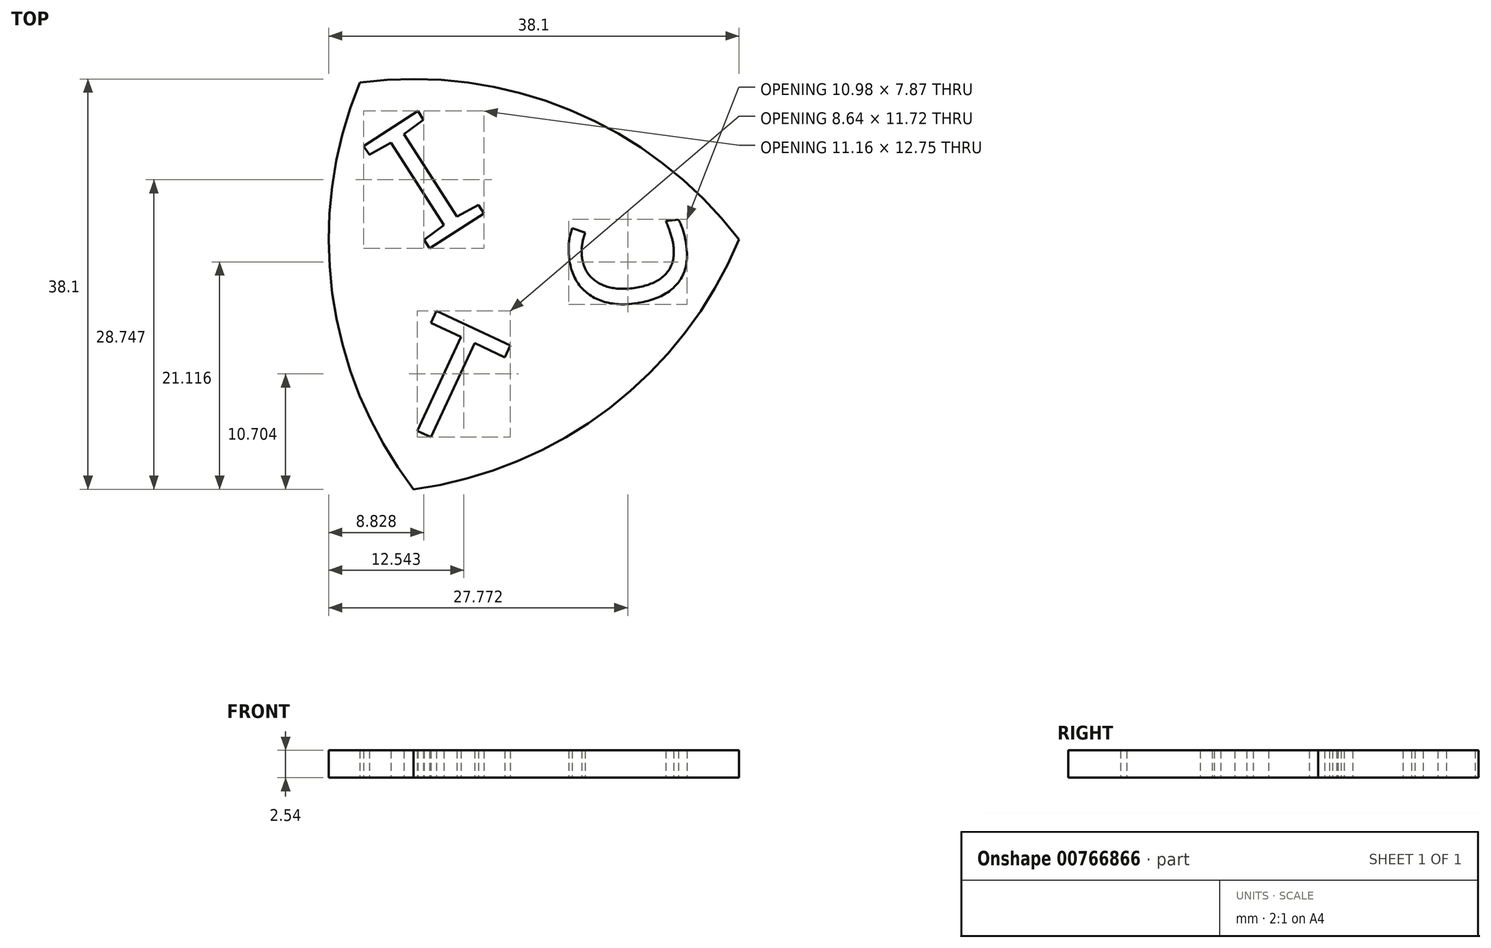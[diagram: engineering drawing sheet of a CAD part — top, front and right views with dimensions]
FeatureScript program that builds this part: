
annotation { "Feature Type Name" : "Feature", "Feature Type Description" : "" }
export const myFeature = defineFeature(function(context is Context, id is Id, definition is map)
    precondition{}
    {
        {
            var Q0;
            Q0=qCreatedBy(makeId("Top.planeOp"),FACE);
            var sketch = newSketch(context, id + "F0", { "sketchPlane" : qUnion([Q0])});
            skCircle(sketch, "E0", {"center": v(0, 0) * mm, "radius": 38.1 * mm});
            skSolve(sketch);
        }
        {
            var Q0;
            Q0=qCreatedBy(makeId("Top.planeOp"),FACE);
            var sketch = newSketch(context, id + "F1", { "sketchPlane" : qUnion([Q0])});
            skCircle(sketch, "E1", {"center": v(-35.2, 14.57) * mm, "radius": 38.1 * mm});
            skSolve(sketch);
        }
        {
            var Q0;
            Q0=qCreatedBy(makeId("Top.planeOp"),FACE);
            var sketch = newSketch(context, id + "F2", { "sketchPlane" : qUnion([Q0])});
            skCircle(sketch, "E2", {"center": v(-30.22, -23.2) * mm, "radius": 38.1 * mm});
            skSolve(sketch);
        }
        {
            var Q0;
            Q0=makeQuery(id+"F2.imprint","IMPRINT",FACE,{"disambiguationData":[TD([[makeQuery(id+"F2.imprint","IMPRINT",EDGE,{"derivedFrom":sQuery(id+"F2.wireOp",EDGE,"E2")}),1.0]])]});
            var Q1;
            Q1=makeQuery(id+"F1.imprint","IMPRINT",FACE,{"disambiguationData":[TD([[makeQuery(id+"F1.imprint","IMPRINT",EDGE,{"derivedFrom":sQuery(id+"F1.wireOp",EDGE,"E1")}),1.0]])]});
            var Q2;
            Q2=makeQuery(id+"F0.imprint","IMPRINT",FACE,{"disambiguationData":[TD([[makeQuery(id+"F0.imprint","IMPRINT",EDGE,{"derivedFrom":sQuery(id+"F0.wireOp",EDGE,"E0")}),1.0]])]});
            extrude(context, id + "F3", {"entities" : qUnion([Q0, Q1, Q2]), "depth" : 2.54 * mm, "offsetDistance" : 25.4 * mm});
        }
        {
            var Q0;
            Q0=makeQuery(id+"F3.opExtrude","SWEPT_BODY",BODY,{"disambiguationData":[OSD([sQuery(id+"F2.wireOp",EDGE,"E2")])]});
            var Q1;
            Q1=makeQuery(id+"F3.opExtrude","SWEPT_BODY",BODY,{"disambiguationData":[OSD([sQuery(id+"F1.wireOp",EDGE,"E1")])]});
            var Q2;
            Q2=makeQuery(id+"F3.opExtrude","SWEPT_BODY",BODY,{"disambiguationData":[OSD([sQuery(id+"F0.wireOp",EDGE,"E0")])]});
            booleanBodies(context, id + "F4", {"operationType" : BooleanOperationType.INTERSECTION, "tools" : qUnion([Q0, Q1, Q2])});
        }
        {
            var Q0;
            Q0=qCreatedBy(makeId("Top.planeOp"),FACE);
            var sketch = newSketch(context, id + "F5", { "sketchPlane" : qUnion([Q0])});
            skText(sketch, "E3", { "text": "C", "fontName": "DroidSansMono.ttf"});
            skText(sketch, "E4", { "text": "I", "fontName": "DroidSansMono.ttf"});
            skText(sketch, "E5", { "text": "T", "fontName": "DroidSansMono.ttf"});
            const initialGuessF5  = {"E3": [-0.00434, -0.00623, -0.12316, 0.99239, 0.01073], "E4": [-0.0302, -0.00177, 0.84102, 0.54101, 0.0114], "E5": [-0.03337, -0.01614, 0.9063, -0.42262, 0.01093]};
            skSetInitialGuess(sketch, initialGuessF5);
            skSolve(sketch);
        }
        {
            var Q0;
            Q0 = qSketchRegion(id + "F5", true);
            extrude(context, id + "F6", {"entities" : qUnion([Q0]), "depth" : 2.54 * mm, "offsetDistance" : 25.4 * mm});
        }
        {
            var Q0;
            Q0=makeQuery(id+"F6.opExtrude","SWEPT_BODY",BODY,{"disambiguationData":[OSD([sQuery(id+"F5.wireOp",EDGE,"E3.sketch_text.stroke-0"),sQuery(id+"F5.wireOp",EDGE,"E3.sketch_text.stroke-1"),sQuery(id+"F5.wireOp",EDGE,"E3.sketch_text.stroke-2"),sQuery(id+"F5.wireOp",EDGE,"E3.sketch_text.stroke-3"),sQuery(id+"F5.wireOp",EDGE,"E3.sketch_text.stroke-4"),sQuery(id+"F5.wireOp",EDGE,"E3.sketch_text.stroke-5"),sQuery(id+"F5.wireOp",EDGE,"E3.sketch_text.stroke-6"),sQuery(id+"F5.wireOp",EDGE,"E3.sketch_text.stroke-7"),sQuery(id+"F5.wireOp",EDGE,"E3.sketch_text.stroke-8"),sQuery(id+"F5.wireOp",EDGE,"E3.sketch_text.stroke-9"),sQuery(id+"F5.wireOp",EDGE,"E3.sketch_text.stroke-10"),sQuery(id+"F5.wireOp",EDGE,"E3.sketch_text.stroke-11"),sQuery(id+"F5.wireOp",EDGE,"E3.sketch_text.stroke-12"),sQuery(id+"F5.wireOp",EDGE,"E3.sketch_text.stroke-13")])]});
            var Q1;
            Q1=makeQuery(id+"F6.opExtrude","SWEPT_BODY",BODY,{"disambiguationData":[OSD([sQuery(id+"F5.wireOp",EDGE,"E5.sketch_text.stroke-0"),sQuery(id+"F5.wireOp",EDGE,"E5.sketch_text.stroke-1"),sQuery(id+"F5.wireOp",EDGE,"E5.sketch_text.stroke-2"),sQuery(id+"F5.wireOp",EDGE,"E5.sketch_text.stroke-3"),sQuery(id+"F5.wireOp",EDGE,"E5.sketch_text.stroke-4"),sQuery(id+"F5.wireOp",EDGE,"E5.sketch_text.stroke-5"),sQuery(id+"F5.wireOp",EDGE,"E5.sketch_text.stroke-6"),sQuery(id+"F5.wireOp",EDGE,"E5.sketch_text.stroke-7")])]});
            var Q2;
            Q2=makeQuery(id+"F6.opExtrude","SWEPT_BODY",BODY,{"disambiguationData":[OSD([sQuery(id+"F5.wireOp",EDGE,"E4.sketch_text.stroke-0"),sQuery(id+"F5.wireOp",EDGE,"E4.sketch_text.stroke-1"),sQuery(id+"F5.wireOp",EDGE,"E4.sketch_text.stroke-2"),sQuery(id+"F5.wireOp",EDGE,"E4.sketch_text.stroke-3"),sQuery(id+"F5.wireOp",EDGE,"E4.sketch_text.stroke-4"),sQuery(id+"F5.wireOp",EDGE,"E4.sketch_text.stroke-5"),sQuery(id+"F5.wireOp",EDGE,"E4.sketch_text.stroke-6"),sQuery(id+"F5.wireOp",EDGE,"E4.sketch_text.stroke-7"),sQuery(id+"F5.wireOp",EDGE,"E4.sketch_text.stroke-8"),sQuery(id+"F5.wireOp",EDGE,"E4.sketch_text.stroke-9"),sQuery(id+"F5.wireOp",EDGE,"E4.sketch_text.stroke-10"),sQuery(id+"F5.wireOp",EDGE,"E4.sketch_text.stroke-11")])]});
            var Q3;
            Q3=makeQuery(id+"F4.opBoolean","INTERSECT",BODY,{"derivedFrom":[makeQuery(id+"F3.opExtrude","SWEPT_BODY",BODY,{"disambiguationData":[OSD([sQuery(id+"F0.wireOp",EDGE,"E0")])]}),makeQuery(id+"F3.opExtrude","SWEPT_BODY",BODY,{"disambiguationData":[OSD([sQuery(id+"F1.wireOp",EDGE,"E1")])]}),makeQuery(id+"F3.opExtrude","SWEPT_BODY",BODY,{"disambiguationData":[OSD([sQuery(id+"F2.wireOp",EDGE,"E2")])]})]});
            booleanBodies(context, id + "F7", {"operationType" : BooleanOperationType.SUBTRACTION, "tools" : qUnion([Q0, Q1, Q2]), "targets" : qUnion([Q3])});
        }
    });
